FCSTD DOCUMENT  (FreeCAD 0.19R0.19.2)
Label: 003MainAttatchmentSketch
License: All rights reserved
LicenseURL: http://en.wikipedia.org/wiki/All_rights_reserved
objects: Sketcher::SketchObject×1
note: 1 computed .brp shape members not serialized (recipe doc carries the construction recipe); baked Part::Feature solids carry a one-line shape summary decoded from their .brp

FEATURE [Sketcher::SketchObject] Sketch
  FullyConstrained = true
  sketch-geometry (31):
    g0: Circle CenterX=-16.25 CenterY=0 CenterZ=0 NormalX=0 NormalY=0 NormalZ=1 AngleXU=0 Radius=1.5
    g1: Circle CenterX=16.25 CenterY=0 CenterZ=0 NormalX=0 NormalY=0 NormalZ=1 AngleXU=0 Radius=1.5
    g2: LineSegment StartX=21.05 StartY=0 StartZ=0 EndX=21.05 EndY=-1 EndZ=0
    g3: LineSegment StartX=21.05 StartY=-1 StartZ=0 EndX=21.05 EndY=-4.3 EndZ=0
    g4: LineSegment StartX=16.25 StartY=-4.3 StartZ=0 EndX=21.05 EndY=-4.3 EndZ=0
    g5: LineSegment StartX=16.25 StartY=-4.3 StartZ=0 EndX=13.65 EndY=-4.3 EndZ=0
    g6: LineSegment StartX=-21.05 StartY=0 StartZ=0 EndX=-21.05 EndY=-1 EndZ=0
    g7: LineSegment StartX=-21.05 StartY=-1 StartZ=0 EndX=-21.05 EndY=-4.3 EndZ=0
    g8: LineSegment StartX=-21.05 StartY=-4.3 StartZ=0 EndX=-16.25 EndY=-4.3 EndZ=0
    g9: LineSegment StartX=-13.65 StartY=-4.3 StartZ=0 EndX=-16.25 EndY=-4.3 EndZ=0
    g10: LineSegment StartX=-16.25 StartY=4.3 StartZ=0 EndX=21.05 EndY=4.3 EndZ=0
    g11: LineSegment StartX=-16.25 StartY=4.3 StartZ=0 EndX=-21.05 EndY=4.3 EndZ=0
    g12: LineSegment StartX=-21.05 StartY=0 StartZ=0 EndX=-21.05 EndY=4.3 EndZ=0
    g13: LineSegment StartX=21.05 StartY=0 StartZ=0 EndX=21.05 EndY=4.3 EndZ=0
    g14: LineSegment StartX=-13.65 StartY=-4.3 StartZ=0 EndX=-14.55 EndY=-4.3 EndZ=0
    g15: LineSegment StartX=14.55 StartY=-4.3 StartZ=0 EndX=13.65 EndY=-4.3 EndZ=0
    g16-g19: Circle x4 (B-spline internal-alignment scaffolding for g20; pole/knot coordinates omitted)
    g20: BSplineCurve PolesCount=4 KnotsCount=2 Degree=3 IsPeriodic=0
    g21: GeomPoint X=-10.05 Y=-1 Z=0
    g22: GeomPoint X=-14.55 Y=-4.3 Z=0
    g23-g26: Circle x4 (B-spline internal-alignment scaffolding for g27; pole/knot coordinates omitted)
    g27: BSplineCurve PolesCount=4 KnotsCount=2 Degree=3 IsPeriodic=0
    g28: GeomPoint X=10.05 Y=-1 Z=0
    g29: GeomPoint X=14.55 Y=-4.3 Z=0
    g30: LineSegment StartX=10.05 StartY=-1 StartZ=0 EndX=-10.05 EndY=-1 EndZ=0
  constraints (62):
    c: Block(g1)
    c: Block(g0)
    c: Vertical(g2)
    c: Coincident(g3,g2)
    c: Vertical(g3)
    c: Block(g2)
    c: Horizontal(g4)
    c: Coincident(g4,g3)
    c: Horizontal(g5)
    c: Distance(g5) = 2.6
    c: Vertical(g6)
    c: Block(g6)
    c: Vertical(g7)
    c: Coincident(g7,g6)
    c: Distance(g7) = 3.3
    c: Horizontal(g8)
    c: Coincident(g8,g7)
    c: Distance(g8) = 4.8
    c: Horizontal(g9)
    c: Equal(g5,g9) = 2.6
    c: Coincident(g9,g8)
    c: Horizontal(g10)
    c: Horizontal(g11)
    c: Vertical(g12)
    c: Coincident(g12,g11)
    c: Vertical(g13)
    c: Coincident(g13,g10)
    c: Block(g10)
    c: Block(g12)
    c: Block(g11)
    c: Block(g13)
    c: Block(g4)
    c: Block(g5)
    c: Horizontal(g14)
    c: Distance(g14) = 0.9
    c: Horizontal(g15)
    c: Equal(g14,g15) = 0.9
    c: Coincident(g14,g9)
    c: Coincident(g15,g5)
    c: Weight(g16) = 1
    c: Equal(g16,g17)
    c: Equal(g16,g18)
    c: Coincident(g18,g9)
    c: Equal(g16,g19)
    c: Coincident(g20,g14)
    c: InternalAlignment(g16-g19 -> g20) x4
    c: InternalAlignment(g21,g20)
    c: InternalAlignment(g22,g20)
    c: Weight(g23) = 1
    c: Equal(g23,g24)
    c: Equal(g23,g25)
    c: Coincident(g25,g5)
    c: Equal(g23,g26)
    c: Coincident(g27,g15)
    c: InternalAlignment(g23-g26 -> g27) x4
    c: InternalAlignment(g28,g27)
    c: InternalAlignment(g29,g27)
    c: Block(g27)
    c: Block(g20)
    c: Coincident(g30,g27)
    c: Coincident(g30,g20)
    c: Horizontal(g30)
